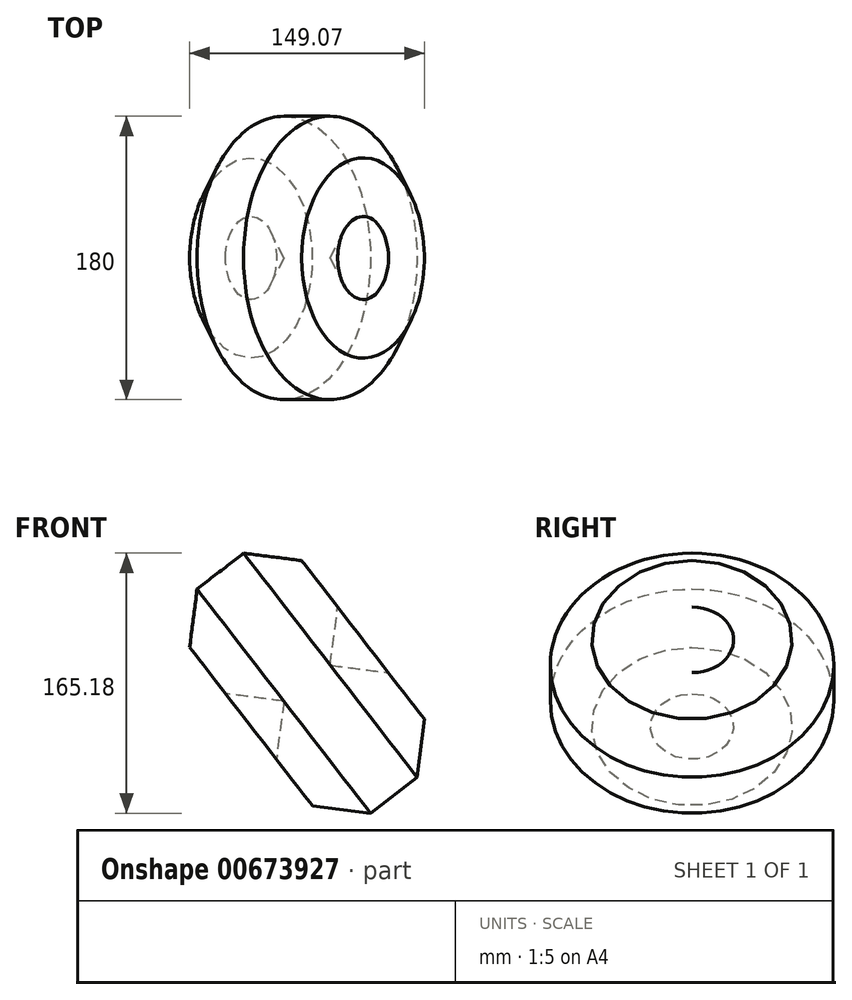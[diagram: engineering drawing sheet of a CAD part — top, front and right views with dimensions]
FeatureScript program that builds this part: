
annotation { "Feature Type Name" : "Feature", "Feature Type Description" : "" }
export const myFeature = defineFeature(function(context is Context, id is Id, definition is map)
    precondition{}
    {
        {
            var Q0;
            Q0=qCreatedBy(makeId("Front.planeOp"),FACE);
            var sketch = newSketch(context, id + "F0", { "sketchPlane" : qUnion([Q0])});
            skPoint(sketch, "E0.0", {"position": v(0, 0) * mm});
            skCircle(sketch, "E1.cCircle", {"center": v(0, 0) * mm, "radius": 48.7 * mm, "construction": true});
            skLineSegment(sketch, "E1.0", {"start": v(42.28, -24.18) * mm, "end": v(12.8, -47) * mm});
            skLineSegment(sketch, "E1.1", {"start": v(12.8, -47) * mm, "end": v(-24.18, -42.28) * mm});
            skLineSegment(sketch, "E1.2", {"start": v(-24.18, -42.28) * mm, "end": v(-47, -12.8) * mm});
            skLineSegment(sketch, "E1.3", {"start": v(-47, -12.8) * mm, "end": v(-42.28, 24.18) * mm});
            skLineSegment(sketch, "E1.4", {"start": v(-42.28, 24.18) * mm, "end": v(-12.8, 47) * mm});
            skLineSegment(sketch, "E1.5", {"start": v(-12.8, 47) * mm, "end": v(24.18, 42.28) * mm});
            skLineSegment(sketch, "E1.6", {"start": v(24.18, 42.28) * mm, "end": v(47, 12.8) * mm});
            skLineSegment(sketch, "E1.7", {"start": v(47, 12.8) * mm, "end": v(42.28, -24.18) * mm});
            skSolve(sketch);
        }
        {
            var Q0;
            Q0=makeQuery(id+"F0.imprint","IMPRINT",FACE,{"disambiguationData":[TD([[makeQuery(id+"F0.imprint","IMPRINT",EDGE,{"derivedFrom":sQuery(id+"F0.wireOp",EDGE,"E1.0")}),-1.0]])]});
            var Q1;
            Q1=sQuery(id+"F0.wireOp",EDGE,"E1.4");
            revolve(context, id + "F1", {"entities" : qUnion([Q0]), "axis" : qUnion([Q1]), "revolveType" : RevolveType.FULL});
        }
    });
